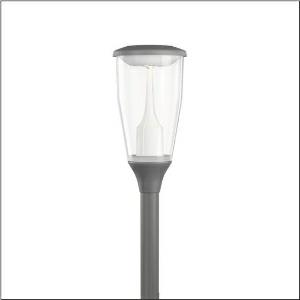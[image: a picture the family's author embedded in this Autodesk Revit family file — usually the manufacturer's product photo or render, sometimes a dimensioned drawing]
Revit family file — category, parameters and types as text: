
# Revit family: dl_11_iq___p1_0a_5xa5565bf14h000022_0962
name_source: partatom
category: Lighting Fixtures
units: mm (PartAtom-declared; Revit-internal decimal feet)

## family parameters
Cut with Voids When Loaded = No
Host = Face
Light Source = No
Part Type = Normal
Room Calculation Point = No
Round Connector Dimension = Use Diameter
Shared = No

## types (1)
- --- (1 x LED, 1530 lm, 12.9 W, 2200K)
    Apparent Load = 13 VA
    CIE Flux Codes = 34 63 91 95 100
    Color Rendering = 70
    Color Temperature = 2200K
    Default Elevation = 1800 mm
    Description = DL 11 iQ, mast luminaire, Module 540 iQ-SR, primary light control with 3 zone facetted reflector, of plastic, silver coated, highly specular, structured, primary optical cover: cover, of PMMA, transparent, light distribution: P1.0a, light emission: direct distribution, primary light characteristic: asymmetric, installation type: post-top, LED, High Power LED, rated luminous flux: 1.560lm, luminous efficacy: 149lm/W, light colour: 722, colour temperature: 2200K, control gear: iQ Street-Remote, control: Street-Remote, Auto-Match, Temp-Guard, Lumen-Switch, Night-Set, Smart-Wire, Light-Fading, Desk-Remote (wireless, voltage-free reading and setting of iQ features in the workshop via application-optimized NFC function/RFID function), optimised constant luminous flux control (CLO 2.0), mains connection: 220..240V, AC, 50/60Hz, connection cable pre-assembled, cable length: 5,5m, start of lifetime: 13W, end of service life: 13W, reduction: 5W, luminaire housing, upper part, of diecast aluminium, coated, Siteco® metallic grey (DB 702S), spigot size: 60mm (post-top), mounting height: 3..5m, post-top mast mounting element, of diecast aluminium, coated, Siteco® metallic grey (DB 702S), Module 540 iQ-SR, traffic white (RAL 9016), equipment: standard, protection rating (complete): IP66, insulation class (complete): insulation class II (safety insulation), certification: CE, ENEC, ENEC+, VDE, impact resistance: IK07, packaging unit: 1 piece

Light Distribution: P1.0a
    Height = 665 mm
    Lamp = 1 x LED
    Lamp Light Flux = 1530 lm
    Lamp Power = 12.9 W
    Lamp count = 1
    Length = 334 mm
    Luminous efficacy = 119 lm/W
    Manufacturer = Siteco
    ModVariant = No
    Model = 5XA5565BF14H000022
    Number of Poles = 1
    OnlyDefault = Yes
    Power Factor = 1
    Product Name = DL 11 iQ | P1.0a
    Product group = mast luminaire | pylon top
    ProductGroupID = 6100
    Protection Class = Protection class II
    Protection Degree = IP 66
    RLX_Detail_Level = 1
    RLX_Emergency_Light_Flux = 0 lm
    RLX_Emergency_Type = 0
    RLX_Emergency_Type_DB = No
    RlxData = <blob elided: 104729 chars, md5=6e0af030>
    Socket = socket
    Standby Power = 0 W
    System Light Flux = 1530 lm
    System Power = 13 W
    Type Comments = factory setting: luminous flux: 100 % | dim-lin: 254 | 516 mA
    Type Image = l_1258354.jpg
    URL = http://relux.com
    VarID = @adj_113443
    Voltage = 0 V
    Weight = 0.00 kg
    Width = 0 mm  [stored 0 ft]

note: [stored X ft] marks values corroborated as IEEE doubles in the binary element streams (Revit-internal decimal feet)

## geometry (parser evidence)
native form markers: Blend x4, Sweep x11
no freeform markers — native parametric forms only
